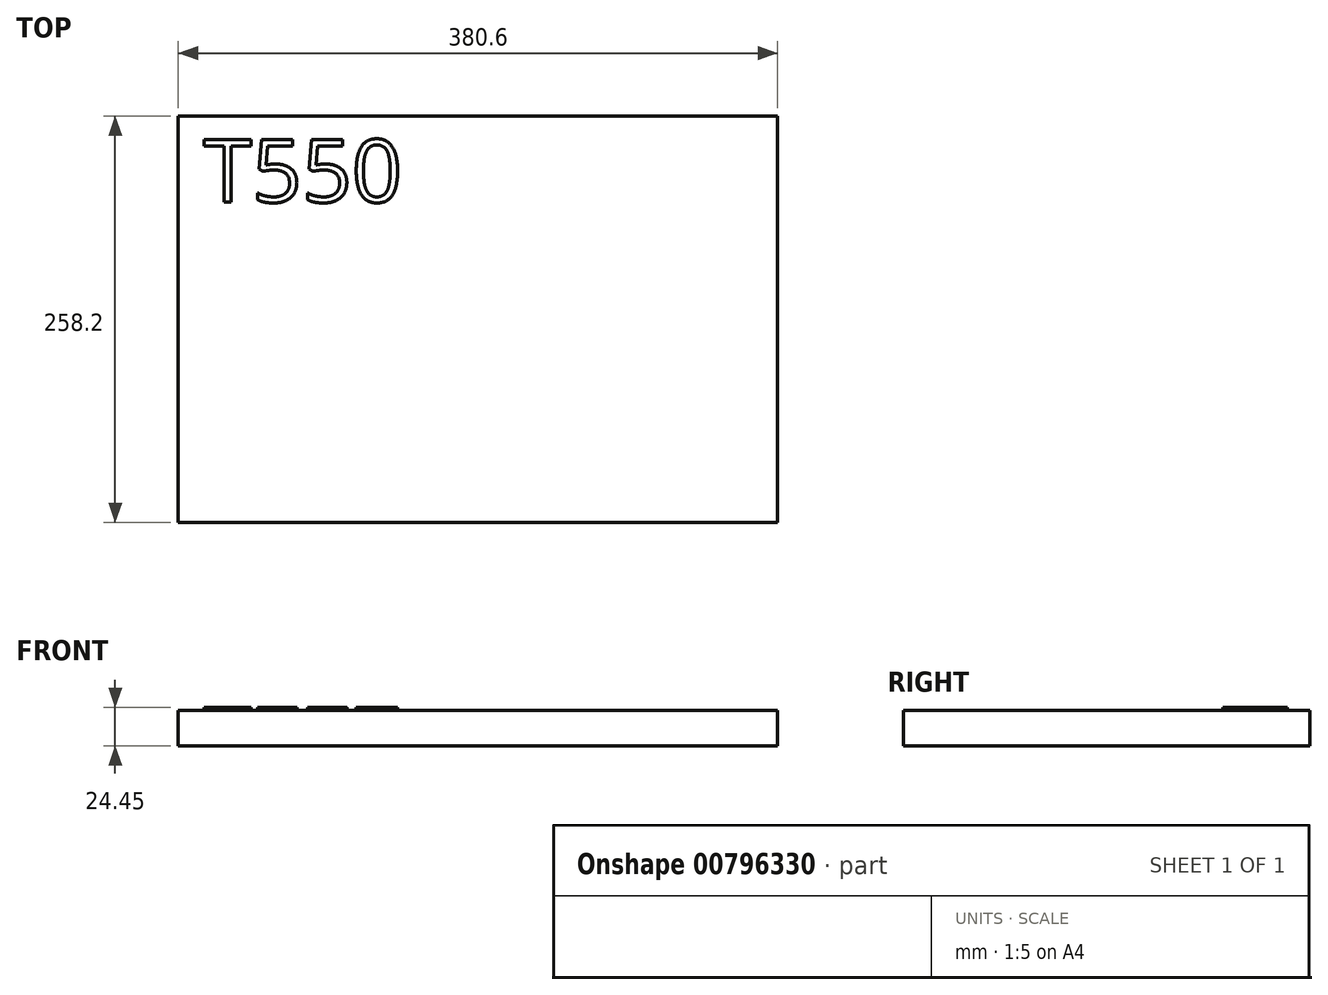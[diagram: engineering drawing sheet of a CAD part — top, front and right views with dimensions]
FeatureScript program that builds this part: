
annotation { "Feature Type Name" : "Feature", "Feature Type Description" : "" }
export const myFeature = defineFeature(function(context is Context, id is Id, definition is map)
    precondition{}
    {
        {
            var Q0;
            Q0=qCreatedBy(makeId("Top.planeOp"),FACE);
            var sketch = newSketch(context, id + "F0", { "sketchPlane" : qUnion([Q0])});
            skLineSegment(sketch, "E0.bottom", {"start": v(-186, 107.7) * mm, "end": v(194.6, 107.7) * mm});
            skLineSegment(sketch, "E0.top", {"start": v(-186, -150.5) * mm, "end": v(194.6, -150.5) * mm});
            skLineSegment(sketch, "E0.left", {"start": v(-186, 107.7) * mm, "end": v(-186, -150.5) * mm});
            skLineSegment(sketch, "E0.right", {"start": v(194.6, 107.7) * mm, "end": v(194.6, -150.5) * mm});
            skSolve(sketch);
        }
        {
            var Q0;
            Q0=makeQuery(id+"F0.imprint","IMPRINT",FACE,{"disambiguationData":[TD([[makeQuery(id+"F0.imprint","IMPRINT",EDGE,{"derivedFrom":sQuery(id+"F0.wireOp",EDGE,"E0.bottom")}),-1.0]])]});
            extrude(context, id + "F1", {"entities" : qUnion([Q0]), "depth" : 22.45 * mm, "offsetDistance" : 25 * mm});
        }
        {
            var Q0;
            Q0=makeQuery(id+"F1.opExtrude","CAP_FACE",FACE,{"disambiguationData":[OSD([sQuery(id+"F0.wireOp",EDGE,"E0.bottom"),sQuery(id+"F0.wireOp",EDGE,"E0.top"),sQuery(id+"F0.wireOp",EDGE,"E0.left"),sQuery(id+"F0.wireOp",EDGE,"E0.right")])],"isStart":false});
            var sketch = newSketch(context, id + "F2", { "sketchPlane" : qUnion([Q0])});
            skText(sketch, "E1", { "text": "T550", "fontName": "OpenSans-Regular.ttf"});
            const initialGuessF2  = {"E1": [-0.16996, 0.05294, 1, 0, 0.04]};
            skSetInitialGuess(sketch, initialGuessF2);
            skSolve(sketch);
        }
        {
            var Q0;
            Q0=qSketchRegion(id+"F2",true);
            extrude(context, id + "F3", {"entities" : qUnion([Q0]), "operationType" : NewBodyOperationType.ADD, "depth" : 2 * mm, "offsetDistance" : 25 * mm});
        }
    });
